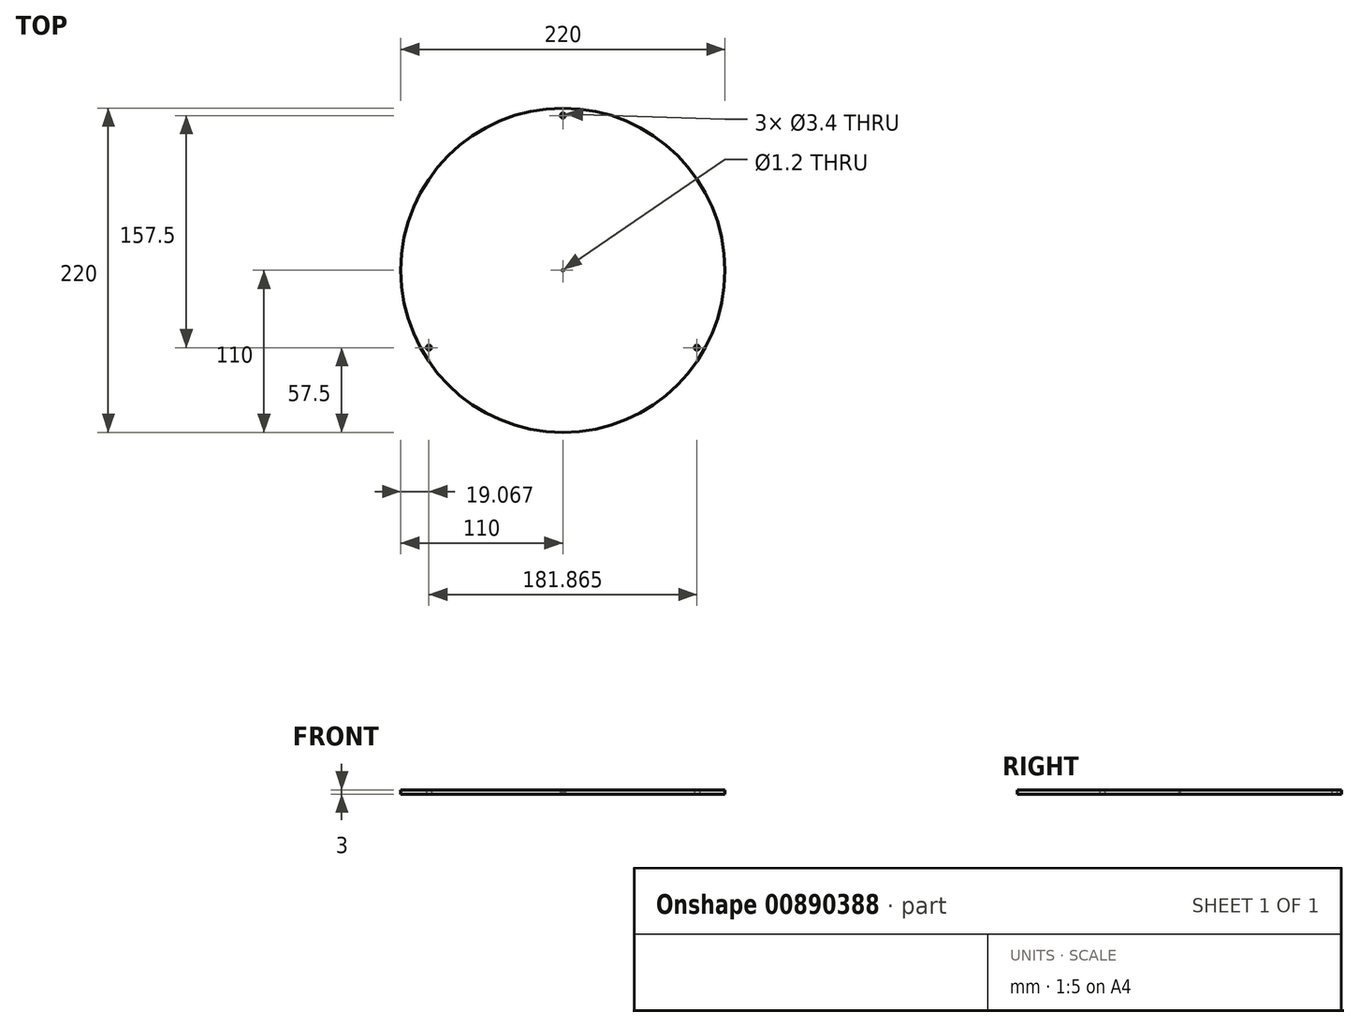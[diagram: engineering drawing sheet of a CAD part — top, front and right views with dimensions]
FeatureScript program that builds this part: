
annotation { "Feature Type Name" : "Feature", "Feature Type Description" : "" }
export const myFeature = defineFeature(function(context is Context, id is Id, definition is map)
    precondition{}
    {
        {
            var Q0;
            Q0=qCreatedBy(makeId("Top.planeOp"),FACE);
            var sketch = newSketch(context, id + "F0", { "sketchPlane" : qUnion([Q0])});
            skCircle(sketch, "E0", {"center": v(0, 0) * mm, "radius": 110 * mm});
            skCircle(sketch, "E1", {"center": v(0, 105) * mm, "radius": 1.7 * mm});
            skCircle(sketch, "E2.1.0", {"center": v(-90.93, -52.5) * mm, "radius": 1.7 * mm});
            skCircle(sketch, "E2.2.0", {"center": v(90.93, -52.5) * mm, "radius": 1.7 * mm});
            skCircle(sketch, "E3", {"center": v(0, 0) * mm, "radius": 0.6 * mm});
            skSolve(sketch);
        }
        {
            var Q0;
            Q0 = qSketchRegion(id + "F0", true);
            extrude(context, id + "F1", {"entities" : qUnion([Q0]), "depth" : 3 * mm, "offsetDistance" : 25 * mm});
        }
    });
